# Revit family: P210876JX-013_JEC4430KB
name_source: partatom
category: Specialty Equipment
units: mm (PartAtom-declared; Revit-internal decimal feet)

## family parameters
Always vertical = Yes
Cut with Voids When Loaded = No
Enable Cutting in Views = No
Maintain Annotation Orientation = No
Part Type = Normal
Room Calculation Point = No
Round Connector Dimension = Use Diameter
Shared = No
Work Plane-Based = No

## types (1)
- JEC4430KB
    Amps = 0 A
    Body Material = ARCAT - Metal - Steel - Stainless
    Cooktop Glass Material = ARCAT - Glass - Tempered - Black Light
    Default Elevation = 0"
    Depth = 21 3/4"
    Description = Oblivion 30" Electric Radiant Cooktop with Emotive Controls
Oblivion 30" Electric Radiant Cooktop with Emotive Controls
    Family Name = Electric Built-In Cooktop
    Feature 1 = Most Powerful Radiant Cooktop In Its Class
Most Powerful Radiant Cooktop In Its Class
    Feature 2 = Versatile Installation
Versatile Installation
    Feature 3 = 12"/9"/6" Triple-Choice™ Element
Élément Triple-Choice™ de 12 po/9 po/6 po
    Height = 5 1/4"
    Installation-Fabrication = https://www.whirlpool.com
https://www.whirlpool.com
    Logo Material = ARCAT - Metal - Steel - White
    Manufacturer = JennAir
    Model = JEC4430KB
    Side Border Material = ARCAT - Metal - Steel - Stainless Black
    Voltage = 0 V
    Width = 30 13/16"

## geometry (parser evidence)
native form markers: Sweep x5
no freeform markers — native parametric forms only
